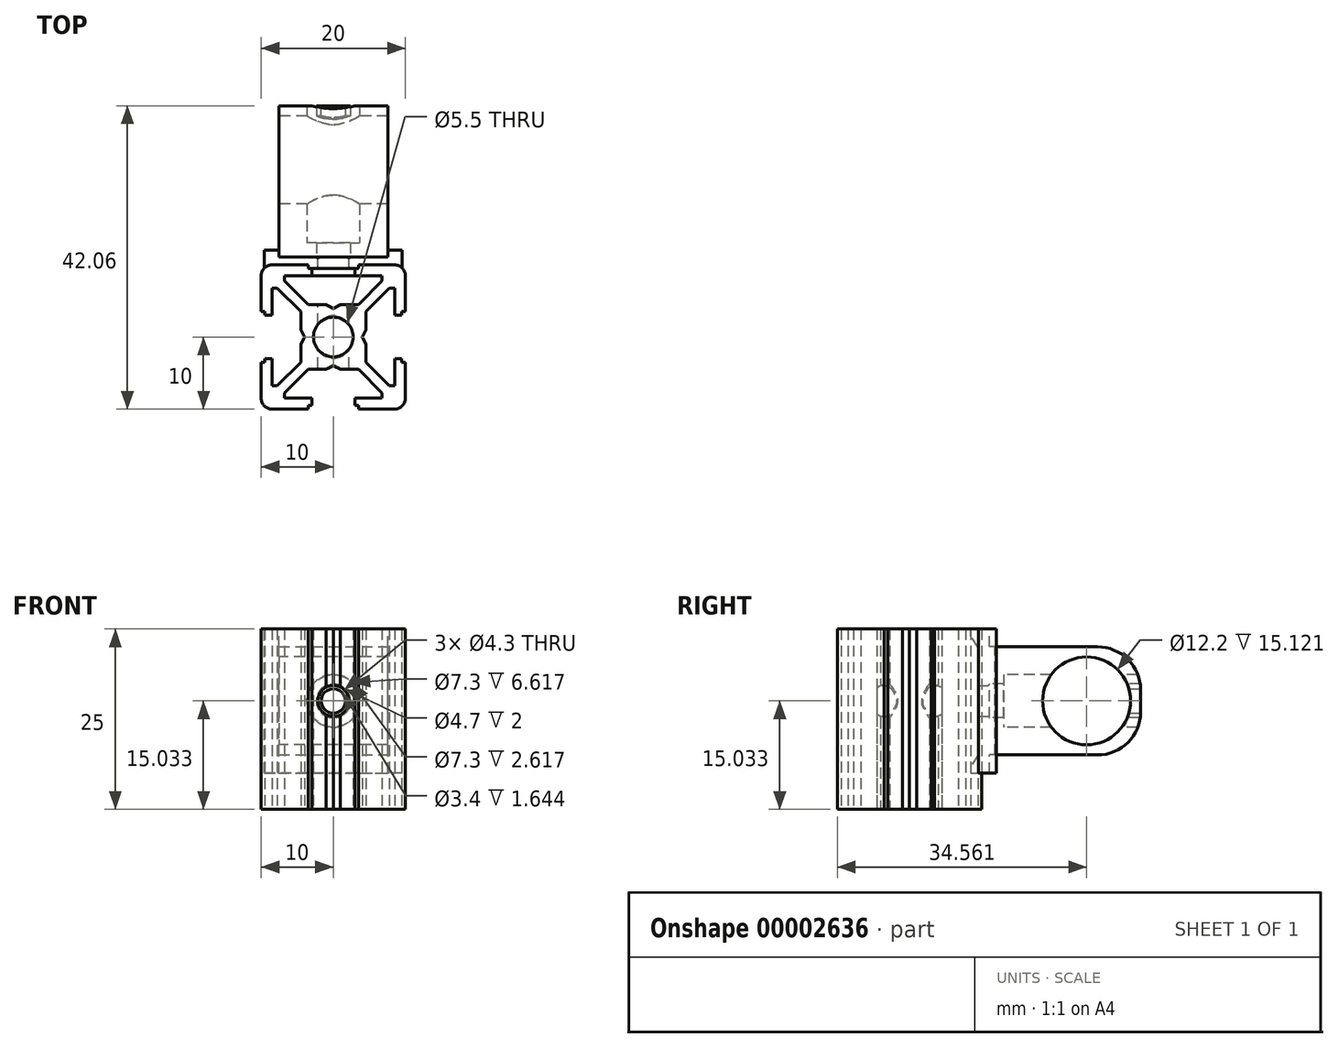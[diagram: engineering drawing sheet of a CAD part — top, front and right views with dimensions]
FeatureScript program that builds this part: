
annotation { "Feature Type Name" : "Feature", "Feature Type Description" : "" }
export const myFeature = defineFeature(function(context is Context, id is Id, definition is map)
    precondition{}
    {
        {
            var Q0;
            Q0=qCreatedBy(makeId("Top.planeOp"),FACE);
            var sketch = newSketch(context, id + "F0", { "sketchPlane" : qUnion([Q0])});
            skLineSegment(sketch, "E0", {"start": v(-1, -4.5) * mm, "end": v(-3.5, -4.5) * mm});
            skLineSegment(sketch, "E1", {"start": v(-6.77, -7.77) * mm, "end": v(-6.77, -8.5) * mm});
            skLineSegment(sketch, "E2", {"start": v(-6.77, -8.5) * mm, "end": v(-3, -8.5) * mm});
            skLineSegment(sketch, "E3", {"start": v(-3, -8.5) * mm, "end": v(-3, -9.5) * mm});
            skLineSegment(sketch, "E4", {"start": v(-5.56, -10) * mm, "end": v(-8.5, -10) * mm});
            skLineSegment(sketch, "E5", {"start": v(-1, -4.5) * mm, "end": v(0, -4) * mm});
            skLineSegment(sketch, "E6", {"start": v(-3, -9.5) * mm, "end": v(-3.5, -9.5) * mm});
            skLineSegment(sketch, "E7", {"start": v(-3.5, -9.5) * mm, "end": v(-3.5, -10) * mm, "construction": true});
            skArc(sketch, "E8.filletArc", {"start": v(-9.56, -9.56) * mm, "mid": v(-9.07, -9.89) * mm, "end": v(-8.5, -10) * mm});
            skLineSegment(sketch, "E9", {"start": v(-3.5, -10) * mm, "end": v(-5.56, -10) * mm});
            skPoint(sketch, "E10.orphan", {"position": v(0, -10) * mm});
            skLineSegment(sketch, "E11.trimOffspring", {"start": v(-8.5, -8.5) * mm, "end": v(-1.94, -1.94) * mm});
            skPoint(sketch, "E12", {"position": v(0, -4.5) * mm});
            skLineSegment(sketch, "E13", {"start": v(-3.5, -4.5) * mm, "end": v(-6.77, -7.77) * mm});
            skArc(sketch, "E14", {"start": v(-1.94, -1.94) * mm, "mid": v(-1.05, -2.54) * mm, "end": v(0, -2.75) * mm});
            skPoint(sketch, "E15", {"position": v(-1.94, -1.94) * mm});
            skLineSegment(sketch, "E16", {"start": v(0, -4) * mm, "end": v(0, -2.75) * mm});
            skLineSegment(sketch, "E17", {"start": v(-9.56, -9.56) * mm, "end": v(-8.5, -8.5) * mm});
            skPoint(sketch, "E18", {"position": v(-5.56, -10) * mm});
            skLineSegment(sketch, "E19", {"start": v(-3.5, -9.5) * mm, "end": v(-3.5, -10) * mm});
            skPoint(sketch, "E20.0.MirrorP", {"position": v(-10, -5.56) * mm});
            skPoint(sketch, "E20.1.MirrorP", {"position": v(-10, -5.56) * mm});
            skPoint(sketch, "E20.2.MirrorP", {"position": v(-10, -5.56) * mm});
            skPoint(sketch, "E20.3.MirrorP", {"position": v(-10, -5.56) * mm});
            skPoint(sketch, "E20.4.MirrorP", {"position": v(-10, -5.56) * mm});
            skPoint(sketch, "E20.5.MirrorP", {"position": v(-10, -5.56) * mm});
            skPoint(sketch, "E20.6.MirrorP", {"position": v(-10, -5.56) * mm});
            skPoint(sketch, "E20.7.MirrorP", {"position": v(-10, -5.56) * mm});
            skPoint(sketch, "E20.8.MirrorP", {"position": v(-10, -5.56) * mm});
            skPoint(sketch, "E20.9.MirrorP", {"position": v(-10, -5.56) * mm});
            skPoint(sketch, "E20.10.MirrorP", {"position": v(-10, -5.56) * mm});
            skLineSegment(sketch, "E20.11.MirrorCS", {"start": v(-9.5, -3.5) * mm, "end": v(-10, -3.5) * mm, "construction": true});
            skPoint(sketch, "E20.12.MirrorP", {"position": v(-10, -5.56) * mm});
            skLineSegment(sketch, "E20.13.MirrorCS", {"start": v(-9.5, -3.5) * mm, "end": v(-10, -3.5) * mm});
            skLineSegment(sketch, "E20.14.MirrorCS", {"start": v(-7.77, -6.77) * mm, "end": v(-8.5, -6.77) * mm});
            skPoint(sketch, "E20.15.MirrorP", {"position": v(-10, -5.56) * mm});
            skLineSegment(sketch, "E20.16.MirrorCS", {"start": v(-9.5, -3) * mm, "end": v(-9.5, -3.5) * mm});
            skPoint(sketch, "E20.17.MirrorP", {"position": v(-10, 0) * mm});
            skLineSegment(sketch, "E20.18.MirrorCS", {"start": v(-10, -5.56) * mm, "end": v(-10, -8.5) * mm});
            skArc(sketch, "E20.19.MirrorCS", {"start": v(-1.94, -1.94) * mm, "mid": v(-2.54, -1.05) * mm, "end": v(-2.75, 0) * mm});
            skPoint(sketch, "E20.20.MirrorP", {"position": v(-4.5, 0) * mm});
            skLineSegment(sketch, "E20.21.MirrorCS", {"start": v(-4.5, -3.5) * mm, "end": v(-7.77, -6.77) * mm});
            skLineSegment(sketch, "E20.23.MirrorCS", {"start": v(-4.5, -1) * mm, "end": v(-4.5, -3.5) * mm});
            skLineSegment(sketch, "E20.24.MirrorCS", {"start": v(-8.5, -6.77) * mm, "end": v(-8.5, -3) * mm});
            skLineSegment(sketch, "E20.25.MirrorCS", {"start": v(-10, -3.5) * mm, "end": v(-10, -5.56) * mm});
            skLineSegment(sketch, "E20.26.MirrorCS", {"start": v(-4, 0) * mm, "end": v(-2.75, 0) * mm});
            skArc(sketch, "E20.28.MirrorCS", {"start": v(-9.56, -9.56) * mm, "mid": v(-9.89, -9.07) * mm, "end": v(-10, -8.5) * mm});
            skLineSegment(sketch, "E20.29.MirrorCS", {"start": v(-4.5, -1) * mm, "end": v(-4, 0) * mm});
            skLineSegment(sketch, "E20.30.MirrorCS", {"start": v(-10, -5.56) * mm, "end": v(-10, -8.5) * mm});
            skPoint(sketch, "E20.31.MirrorP", {"position": v(-10, -5.56) * mm});
            skLineSegment(sketch, "E20.32.MirrorCS", {"start": v(-8.5, -3) * mm, "end": v(-9.5, -3) * mm});
            skPoint(sketch, "E21.0.MirrorP", {"position": v(-5.56, 10) * mm});
            skPoint(sketch, "E21.1.MirrorP", {"position": v(-10, 5.56) * mm});
            skPoint(sketch, "E21.2.MirrorP", {"position": v(-5.56, 10) * mm});
            skPoint(sketch, "E21.3.MirrorP", {"position": v(-10, 5.56) * mm});
            skPoint(sketch, "E21.4.MirrorP", {"position": v(-5.56, 10) * mm});
            skPoint(sketch, "E21.5.MirrorP", {"position": v(-10, 5.56) * mm});
            skPoint(sketch, "E21.6.MirrorP", {"position": v(-10, 5.56) * mm});
            skPoint(sketch, "E21.7.MirrorP", {"position": v(-5.56, 10) * mm});
            skPoint(sketch, "E21.8.MirrorP", {"position": v(-5.56, 10) * mm});
            skPoint(sketch, "E21.9.MirrorP", {"position": v(-10, 5.56) * mm});
            skPoint(sketch, "E21.10.MirrorP", {"position": v(-5.56, 10) * mm});
            skPoint(sketch, "E21.11.MirrorP", {"position": v(-10, 5.56) * mm});
            skPoint(sketch, "E21.12.MirrorP", {"position": v(-5.56, 10) * mm});
            skPoint(sketch, "E21.13.MirrorP", {"position": v(-10, 5.56) * mm});
            skPoint(sketch, "E21.14.MirrorP", {"position": v(-5.56, 10) * mm});
            skPoint(sketch, "E21.15.MirrorP", {"position": v(-10, 5.56) * mm});
            skPoint(sketch, "E21.16.MirrorP", {"position": v(-5.56, 10) * mm});
            skPoint(sketch, "E21.17.MirrorP", {"position": v(-10, 5.56) * mm});
            skLineSegment(sketch, "E21.18.MirrorCS", {"start": v(-9.5, 3.5) * mm, "end": v(-10, 3.5) * mm, "construction": true});
            skPoint(sketch, "E21.19.MirrorP", {"position": v(-5.56, 10) * mm});
            skPoint(sketch, "E21.20.MirrorP", {"position": v(-10, 5.56) * mm});
            skLineSegment(sketch, "E21.21.MirrorCS", {"start": v(-3.5, 9.5) * mm, "end": v(-3.5, 10) * mm, "construction": true});
            skLineSegment(sketch, "E21.22.MirrorCS", {"start": v(-3.5, 9.5) * mm, "end": v(-3.5, 10) * mm});
            skPoint(sketch, "E21.23.MirrorP", {"position": v(-5.56, 10) * mm});
            skLineSegment(sketch, "E21.24.MirrorCS", {"start": v(-9.5, 3.5) * mm, "end": v(-10, 3.5) * mm});
            skPoint(sketch, "E21.25.MirrorP", {"position": v(-10, 5.56) * mm});
            skPoint(sketch, "E21.26.MirrorP", {"position": v(-5.56, 10) * mm});
            skPoint(sketch, "E21.27.MirrorP", {"position": v(-10, 5.56) * mm});
            skLineSegment(sketch, "E21.28.MirrorCS", {"start": v(-3, 9.5) * mm, "end": v(-3.5, 9.5) * mm});
            skLineSegment(sketch, "E21.29.MirrorCS", {"start": v(-9.5, 3) * mm, "end": v(-9.5, 3.5) * mm});
            skLineSegment(sketch, "E21.30.MirrorCS", {"start": v(-8.5, 3) * mm, "end": v(-9.5, 3) * mm});
            skPoint(sketch, "E21.31.MirrorP", {"position": v(-5.56, 10) * mm});
            skPoint(sketch, "E21.32.MirrorP", {"position": v(-10, 5.56) * mm});
            skLineSegment(sketch, "E21.34.MirrorCS", {"start": v(-10, 3.5) * mm, "end": v(-10, 5.56) * mm});
            skArc(sketch, "E21.35.MirrorCS", {"start": v(-9.56, 9.56) * mm, "mid": v(-9.89, 9.07) * mm, "end": v(-10, 8.5) * mm});
            skLineSegment(sketch, "E21.36.MirrorCS", {"start": v(-8.5, 6.77) * mm, "end": v(-8.5, 3) * mm});
            skLineSegment(sketch, "E21.37.MirrorCS", {"start": v(-4.5, 1) * mm, "end": v(-4, 0) * mm});
            skLineSegment(sketch, "E21.38.MirrorCS", {"start": v(-10, 5.56) * mm, "end": v(-10, 8.5) * mm});
            skLineSegment(sketch, "E21.40.MirrorCS", {"start": v(-4.5, 3.5) * mm, "end": v(-7.77, 6.77) * mm});
            skLineSegment(sketch, "E21.41.MirrorCS", {"start": v(-4.5, 1) * mm, "end": v(-4.5, 3.5) * mm});
            skLineSegment(sketch, "E21.42.MirrorCS", {"start": v(-1, 4.5) * mm, "end": v(-3.5, 4.5) * mm});
            skLineSegment(sketch, "E21.43.MirrorCS", {"start": v(-6.77, 8.5) * mm, "end": v(-3, 8.5) * mm});
            skLineSegment(sketch, "E21.44.MirrorCS", {"start": v(-6.77, 7.77) * mm, "end": v(-6.77, 8.5) * mm});
            skLineSegment(sketch, "E21.45.MirrorCS", {"start": v(-5.56, 10) * mm, "end": v(-8.5, 10) * mm});
            skLineSegment(sketch, "E21.46.MirrorCS", {"start": v(-3, 8.5) * mm, "end": v(-3, 9.5) * mm});
            skLineSegment(sketch, "E21.47.MirrorCS", {"start": v(-1, 4.5) * mm, "end": v(0, 4) * mm});
            skLineSegment(sketch, "E21.48.MirrorCS", {"start": v(-5.56, 10) * mm, "end": v(-8.5, 10) * mm});
            skLineSegment(sketch, "E21.49.MirrorCS", {"start": v(-3.5, 10) * mm, "end": v(-5.56, 10) * mm});
            skArc(sketch, "E21.50.MirrorCS", {"start": v(-9.56, 9.56) * mm, "mid": v(-9.07, 9.89) * mm, "end": v(-8.5, 10) * mm});
            skLineSegment(sketch, "E21.51.MirrorCS", {"start": v(-3.5, 4.5) * mm, "end": v(-6.77, 7.77) * mm});
            skLineSegment(sketch, "E21.52.MirrorCS", {"start": v(-8.5, 8.5) * mm, "end": v(-1.94, 1.94) * mm});
            skLineSegment(sketch, "E21.53.MirrorCS", {"start": v(-9.56, 9.56) * mm, "end": v(-8.5, 8.5) * mm});
            skLineSegment(sketch, "E21.54.MirrorCS", {"start": v(-9.56, 9.56) * mm, "end": v(-8.5, 8.5) * mm});
            skLineSegment(sketch, "E21.55.MirrorCS", {"start": v(0, 4) * mm, "end": v(0, 2.75) * mm});
            skArc(sketch, "E21.56.MirrorCS", {"start": v(-1.94, 1.94) * mm, "mid": v(-1.05, 2.54) * mm, "end": v(0, 2.75) * mm});
            skPoint(sketch, "E21.58.MirrorP", {"position": v(0, 4.5) * mm});
            skLineSegment(sketch, "E21.59.MirrorCS", {"start": v(-7.77, 6.77) * mm, "end": v(-8.5, 6.77) * mm});
            skPoint(sketch, "E21.60.MirrorP", {"position": v(-5.56, 10) * mm});
            skArc(sketch, "E21.61.MirrorCS", {"start": v(-1.94, 1.94) * mm, "mid": v(-2.54, 1.05) * mm, "end": v(-2.75, 0) * mm});
            skPoint(sketch, "E21.62.MirrorP", {"position": v(0, 10) * mm});
            skPoint(sketch, "E21.63.MirrorP", {"position": v(-1.94, 1.94) * mm});
            skPoint(sketch, "E21.64.MirrorP", {"position": v(-1.94, 1.94) * mm});
            skLineSegment(sketch, "E21.65.MirrorCS", {"start": v(-10, 5.56) * mm, "end": v(-10, 8.5) * mm});
            skPoint(sketch, "E21.66.MirrorP", {"position": v(-10, 5.56) * mm});
            skPoint(sketch, "E22.0.MirrorP", {"position": v(10, 5.56) * mm});
            skPoint(sketch, "E22.1.MirrorP", {"position": v(5.56, -10) * mm});
            skPoint(sketch, "E22.2.MirrorP", {"position": v(5.56, 10) * mm});
            skPoint(sketch, "E22.3.MirrorP", {"position": v(10, 5.56) * mm});
            skPoint(sketch, "E22.4.MirrorP", {"position": v(10, -5.56) * mm});
            skPoint(sketch, "E22.5.MirrorP", {"position": v(5.56, -10) * mm});
            skPoint(sketch, "E22.6.MirrorP", {"position": v(5.56, -10) * mm});
            skPoint(sketch, "E22.7.MirrorP", {"position": v(10, 5.56) * mm});
            skPoint(sketch, "E22.8.MirrorP", {"position": v(5.56, 10) * mm});
            skPoint(sketch, "E22.9.MirrorP", {"position": v(10, -5.56) * mm});
            skPoint(sketch, "E22.10.MirrorP", {"position": v(10, 5.56) * mm});
            skPoint(sketch, "E22.11.MirrorP", {"position": v(5.56, -10) * mm});
            skPoint(sketch, "E22.12.MirrorP", {"position": v(5.56, 10) * mm});
            skPoint(sketch, "E22.13.MirrorP", {"position": v(10, -5.56) * mm});
            skPoint(sketch, "E22.14.MirrorP", {"position": v(10, 5.56) * mm});
            skPoint(sketch, "E22.15.MirrorP", {"position": v(5.56, -10) * mm});
            skPoint(sketch, "E22.16.MirrorP", {"position": v(10, -5.56) * mm});
            skPoint(sketch, "E22.17.MirrorP", {"position": v(5.56, 10) * mm});
            skPoint(sketch, "E22.18.MirrorP", {"position": v(5.56, -10) * mm});
            skPoint(sketch, "E22.19.MirrorP", {"position": v(5.56, 10) * mm});
            skPoint(sketch, "E22.20.MirrorP", {"position": v(10, 5.56) * mm});
            skPoint(sketch, "E22.21.MirrorP", {"position": v(10, -5.56) * mm});
            skPoint(sketch, "E22.22.MirrorP", {"position": v(10, -5.56) * mm});
            skPoint(sketch, "E22.23.MirrorP", {"position": v(5.56, -10) * mm});
            skPoint(sketch, "E22.24.MirrorP", {"position": v(10, 5.56) * mm});
            skPoint(sketch, "E22.25.MirrorP", {"position": v(5.56, 10) * mm});
            skPoint(sketch, "E22.26.MirrorP", {"position": v(10, -5.56) * mm});
            skPoint(sketch, "E22.27.MirrorP", {"position": v(10, 5.56) * mm});
            skPoint(sketch, "E22.28.MirrorP", {"position": v(5.56, -10) * mm});
            skPoint(sketch, "E22.29.MirrorP", {"position": v(5.56, 10) * mm});
            skPoint(sketch, "E22.30.MirrorP", {"position": v(10, -5.56) * mm});
            skPoint(sketch, "E22.31.MirrorP", {"position": v(5.56, 10) * mm});
            skPoint(sketch, "E22.32.MirrorP", {"position": v(5.56, -10) * mm});
            skPoint(sketch, "E22.33.MirrorP", {"position": v(10, 5.56) * mm});
            skPoint(sketch, "E22.34.MirrorP", {"position": v(10, 5.56) * mm});
            skPoint(sketch, "E22.35.MirrorP", {"position": v(5.56, 10) * mm});
            skPoint(sketch, "E22.36.MirrorP", {"position": v(10, -5.56) * mm});
            skPoint(sketch, "E22.37.MirrorP", {"position": v(5.56, -10) * mm});
            skLineSegment(sketch, "E22.38.MirrorCS", {"start": v(3.5, 9.5) * mm, "end": v(3.5, 10) * mm, "construction": true});
            skLineSegment(sketch, "E22.39.MirrorCS", {"start": v(9.5, 3.5) * mm, "end": v(10, 3.5) * mm, "construction": true});
            skLineSegment(sketch, "E22.40.MirrorCS", {"start": v(9.5, -3.5) * mm, "end": v(10, -3.5) * mm, "construction": true});
            skLineSegment(sketch, "E22.41.MirrorCS", {"start": v(3.5, -9.5) * mm, "end": v(3.5, -10) * mm, "construction": true});
            skPoint(sketch, "E22.42.MirrorP", {"position": v(10, 5.56) * mm});
            skPoint(sketch, "E22.43.MirrorP", {"position": v(10, -5.56) * mm});
            skPoint(sketch, "E22.44.MirrorP", {"position": v(5.56, -10) * mm});
            skPoint(sketch, "E22.45.MirrorP", {"position": v(5.56, 10) * mm});
            skLineSegment(sketch, "E22.46.MirrorCS", {"start": v(9.5, 3.5) * mm, "end": v(10, 3.5) * mm});
            skLineSegment(sketch, "E22.47.MirrorCS", {"start": v(9.5, -3) * mm, "end": v(9.5, -3.5) * mm});
            skLineSegment(sketch, "E22.48.MirrorCS", {"start": v(9.5, -3.5) * mm, "end": v(10, -3.5) * mm});
            skLineSegment(sketch, "E22.49.MirrorCS", {"start": v(9.56, -9.56) * mm, "end": v(8.5, -8.5) * mm});
            skLineSegment(sketch, "E22.50.MirrorCS", {"start": v(3, -9.5) * mm, "end": v(3.5, -9.5) * mm});
            skPoint(sketch, "E22.51.MirrorP", {"position": v(10, -5.56) * mm});
            skPoint(sketch, "E22.52.MirrorP", {"position": v(10, 5.56) * mm});
            skPoint(sketch, "E22.53.MirrorP", {"position": v(5.56, 10) * mm});
            skPoint(sketch, "E22.54.MirrorP", {"position": v(5.56, -10) * mm});
            skLineSegment(sketch, "E22.55.MirrorCS", {"start": v(3, 9.5) * mm, "end": v(3.5, 9.5) * mm});
            skLineSegment(sketch, "E22.56.MirrorCS", {"start": v(9.5, 3) * mm, "end": v(9.5, 3.5) * mm});
            skLineSegment(sketch, "E22.57.MirrorCS", {"start": v(3.5, -9.5) * mm, "end": v(3.5, -10) * mm});
            skLineSegment(sketch, "E22.58.MirrorCS", {"start": v(3.5, 9.5) * mm, "end": v(3.5, 10) * mm});
            skLineSegment(sketch, "E22.59.MirrorCS", {"start": v(3, 8.5) * mm, "end": v(3, 9.5) * mm});
            skLineSegment(sketch, "E22.60.MirrorCS", {"start": v(6.77, 7.77) * mm, "end": v(6.77, 8.5) * mm});
            skPoint(sketch, "E22.61.MirrorP", {"position": v(5.56, 10) * mm});
            skLineSegment(sketch, "E22.62.MirrorCS", {"start": v(6.77, -7.77) * mm, "end": v(6.77, -8.5) * mm});
            skPoint(sketch, "E22.63.MirrorP", {"position": v(5.56, -10) * mm});
            skPoint(sketch, "E22.64.MirrorP", {"position": v(10, -5.56) * mm});
            skLineSegment(sketch, "E22.65.MirrorCS", {"start": v(9.56, -9.56) * mm, "end": v(8.5, -8.5) * mm});
            skLineSegment(sketch, "E22.66.MirrorCS", {"start": v(7.77, 6.77) * mm, "end": v(8.5, 6.77) * mm});
            skLineSegment(sketch, "E22.67.MirrorCS", {"start": v(1, 4.5) * mm, "end": v(0, 4) * mm});
            skLineSegment(sketch, "E22.68.MirrorCS", {"start": v(4.5, -1) * mm, "end": v(4, 0) * mm});
            skLineSegment(sketch, "E22.69.MirrorCS", {"start": v(4, 0) * mm, "end": v(2.75, 0) * mm});
            skLineSegment(sketch, "E22.70.MirrorCS", {"start": v(1, -4.5) * mm, "end": v(0, -4) * mm});
            skLineSegment(sketch, "E22.71.MirrorCS", {"start": v(10, 5.56) * mm, "end": v(10, 8.5) * mm});
            skPoint(sketch, "E22.72.MirrorP", {"position": v(10, 5.56) * mm});
            skPoint(sketch, "E22.73.MirrorP", {"position": v(10, 0) * mm});
            skLineSegment(sketch, "E22.74.MirrorCS", {"start": v(9.56, 9.56) * mm, "end": v(8.5, 8.5) * mm});
            skLineSegment(sketch, "E22.75.MirrorCS", {"start": v(4.5, 1) * mm, "end": v(4, 0) * mm});
            skLineSegment(sketch, "E22.76.MirrorCS", {"start": v(7.77, -6.77) * mm, "end": v(8.5, -6.77) * mm});
            skLineSegment(sketch, "E22.78.MirrorCS", {"start": v(10, 5.56) * mm, "end": v(10, 8.5) * mm});
            skLineSegment(sketch, "E22.79.MirrorCS", {"start": v(3.5, -10) * mm, "end": v(5.56, -10) * mm});
            skLineSegment(sketch, "E22.80.MirrorCS", {"start": v(3, -8.5) * mm, "end": v(3, -9.5) * mm});
            skLineSegment(sketch, "E22.81.MirrorCS", {"start": v(5.56, -10) * mm, "end": v(8.5, -10) * mm});
            skPoint(sketch, "E22.83.MirrorP", {"position": v(5.56, -10) * mm});
            skLineSegment(sketch, "E22.84.MirrorCS", {"start": v(8.5, 3) * mm, "end": v(9.5, 3) * mm});
            skLineSegment(sketch, "E22.85.MirrorCS", {"start": v(3.5, 10) * mm, "end": v(5.56, 10) * mm});
            skArc(sketch, "E22.86.MirrorCS", {"start": v(1.94, -1.94) * mm, "mid": v(1.05, -2.54) * mm, "end": v(0, -2.75) * mm});
            skPoint(sketch, "E22.87.MirrorP", {"position": v(1.94, -1.94) * mm});
            skPoint(sketch, "E22.88.MirrorP", {"position": v(4.5, 0) * mm});
            skArc(sketch, "E22.89.MirrorCS", {"start": v(9.56, 9.56) * mm, "mid": v(9.07, 9.89) * mm, "end": v(8.5, 10) * mm});
            skLineSegment(sketch, "E22.90.MirrorCS", {"start": v(10, 3.5) * mm, "end": v(10, 5.56) * mm});
            skLineSegment(sketch, "E22.91.MirrorCS", {"start": v(8.5, -8.5) * mm, "end": v(1.94, -1.94) * mm});
            skLineSegment(sketch, "E22.92.MirrorCS", {"start": v(3.5, -4.5) * mm, "end": v(6.77, -7.77) * mm});
            skArc(sketch, "E22.93.MirrorCS", {"start": v(9.56, -9.56) * mm, "mid": v(9.07, -9.89) * mm, "end": v(8.5, -10) * mm});
            skLineSegment(sketch, "E22.94.MirrorCS", {"start": v(6.77, 8.5) * mm, "end": v(3, 8.5) * mm});
            skLineSegment(sketch, "E22.95.MirrorCS", {"start": v(4.5, 1) * mm, "end": v(4.5, 3.5) * mm});
            skLineSegment(sketch, "E22.96.MirrorCS", {"start": v(10, -5.56) * mm, "end": v(10, -8.5) * mm});
            skLineSegment(sketch, "E22.97.MirrorCS", {"start": v(5.56, -10) * mm, "end": v(8.5, -10) * mm});
            skPoint(sketch, "E22.99.MirrorP", {"position": v(5.56, 10) * mm});
            skLineSegment(sketch, "E22.101.MirrorCS", {"start": v(10, -5.56) * mm, "end": v(10, -8.5) * mm});
            skPoint(sketch, "E22.103.MirrorP", {"position": v(4.5, 0) * mm});
            skArc(sketch, "E22.104.MirrorCS", {"start": v(1.94, 1.94) * mm, "mid": v(1.05, 2.54) * mm, "end": v(0, 2.75) * mm});
            skArc(sketch, "E22.105.MirrorCS", {"start": v(1.94, -1.94) * mm, "mid": v(2.54, -1.05) * mm, "end": v(2.75, 0) * mm});
            skLineSegment(sketch, "E22.106.MirrorCS", {"start": v(4.5, 3.5) * mm, "end": v(7.77, 6.77) * mm});
            skLineSegment(sketch, "E22.107.MirrorCS", {"start": v(8.5, 8.5) * mm, "end": v(1.94, 1.94) * mm});
            skLineSegment(sketch, "E22.108.MirrorCS", {"start": v(8.5, -6.77) * mm, "end": v(8.5, -3) * mm});
            skArc(sketch, "E22.109.MirrorCS", {"start": v(9.56, -9.56) * mm, "mid": v(9.89, -9.07) * mm, "end": v(10, -8.5) * mm});
            skPoint(sketch, "E22.110.MirrorP", {"position": v(1.94, 1.94) * mm});
            skLineSegment(sketch, "E22.111.MirrorCS", {"start": v(6.77, -8.5) * mm, "end": v(3, -8.5) * mm});
            skLineSegment(sketch, "E22.112.MirrorCS", {"start": v(1, -4.5) * mm, "end": v(3.5, -4.5) * mm});
            skLineSegment(sketch, "E22.113.MirrorCS", {"start": v(4.5, -1) * mm, "end": v(4.5, -3.5) * mm});
            skLineSegment(sketch, "E22.114.MirrorCS", {"start": v(3.5, 4.5) * mm, "end": v(6.77, 7.77) * mm});
            skPoint(sketch, "E22.115.MirrorP", {"position": v(10, -5.56) * mm});
            skLineSegment(sketch, "E22.116.MirrorCS", {"start": v(9.56, 9.56) * mm, "end": v(8.5, 8.5) * mm});
            skLineSegment(sketch, "E22.117.MirrorCS", {"start": v(4, 0) * mm, "end": v(2.75, 0) * mm});
            skArc(sketch, "E22.118.MirrorCS", {"start": v(9.56, 9.56) * mm, "mid": v(9.89, 9.07) * mm, "end": v(10, 8.5) * mm});
            skPoint(sketch, "E22.119.MirrorP", {"position": v(5.56, 10) * mm});
            skLineSegment(sketch, "E22.120.MirrorCS", {"start": v(8.5, -3) * mm, "end": v(9.5, -3) * mm});
            skLineSegment(sketch, "E22.121.MirrorCS", {"start": v(1, 4.5) * mm, "end": v(3.5, 4.5) * mm});
            skArc(sketch, "E22.122.MirrorCS", {"start": v(1.94, 1.94) * mm, "mid": v(2.54, 1.05) * mm, "end": v(2.75, 0) * mm});
            skLineSegment(sketch, "E22.123.MirrorCS", {"start": v(5.56, 10) * mm, "end": v(8.5, 10) * mm});
            skPoint(sketch, "E22.124.MirrorP", {"position": v(10, 0) * mm});
            skLineSegment(sketch, "E22.125.MirrorCS", {"start": v(10, -3.5) * mm, "end": v(10, -5.56) * mm});
            skLineSegment(sketch, "E22.126.MirrorCS", {"start": v(5.56, 10) * mm, "end": v(8.5, 10) * mm});
            skLineSegment(sketch, "E22.127.MirrorCS", {"start": v(4.5, -3.5) * mm, "end": v(7.77, -6.77) * mm});
            skPoint(sketch, "E22.128.MirrorP", {"position": v(10, -5.56) * mm});
            skPoint(sketch, "E22.129.MirrorP", {"position": v(1.94, -1.94) * mm});
            skPoint(sketch, "E22.131.MirrorP", {"position": v(1.94, 1.94) * mm});
            skLineSegment(sketch, "E22.132.MirrorCS", {"start": v(8.5, 6.77) * mm, "end": v(8.5, 3) * mm});
            skPoint(sketch, "E22.133.MirrorP", {"position": v(10, 5.56) * mm});
            skSolve(sketch);
        }
        {
            var Q0;
            Q0=qSketchRegion(id+"F0",true);
            extrude(context, id + "F1", {"entities" : qUnion([Q0]), "depth" : 25 * mm});
        }
        {
            var Q0;
            Q0=makeQuery(id+"F1.opExtrude","CAP_FACE",FACE,{"disambiguationData":[OSD([sQuery(id+"F0.wireOp",EDGE,"E0"),sQuery(id+"F0.wireOp",EDGE,"E1"),sQuery(id+"F0.wireOp",EDGE,"E2"),sQuery(id+"F0.wireOp",EDGE,"E3"),sQuery(id+"F0.wireOp",EDGE,"E5"),sQuery(id+"F0.wireOp",EDGE,"E6"),sQuery(id+"F0.wireOp",EDGE,"E4"),sQuery(id+"F0.wireOp",EDGE,"E8.filletArc"),sQuery(id+"F0.wireOp",EDGE,"E13"),sQuery(id+"F0.wireOp",EDGE,"E14"),sQuery(id+"F0.wireOp",EDGE,"E19"),sQuery(id+"F0.wireOp",EDGE,"E20.13.MirrorCS"),sQuery(id+"F0.wireOp",EDGE,"E20.14.MirrorCS"),sQuery(id+"F0.wireOp",EDGE,"E20.16.MirrorCS"),sQuery(id+"F0.wireOp",EDGE,"E20.19.MirrorCS"),sQuery(id+"F0.wireOp",EDGE,"E20.21.MirrorCS"),sQuery(id+"F0.wireOp",EDGE,"E20.23.MirrorCS"),sQuery(id+"F0.wireOp",EDGE,"E20.24.MirrorCS"),sQuery(id+"F0.wireOp",EDGE,"E20.25.MirrorCS"),sQuery(id+"F0.wireOp",EDGE,"E20.28.MirrorCS"),sQuery(id+"F0.wireOp",EDGE,"E20.29.MirrorCS"),sQuery(id+"F0.wireOp",EDGE,"E20.32.MirrorCS"),sQuery(id+"F0.wireOp",EDGE,"E21.22.MirrorCS"),sQuery(id+"F0.wireOp",EDGE,"E21.24.MirrorCS"),sQuery(id+"F0.wireOp",EDGE,"E21.28.MirrorCS"),sQuery(id+"F0.wireOp",EDGE,"E21.29.MirrorCS"),sQuery(id+"F0.wireOp",EDGE,"E21.30.MirrorCS"),sQuery(id+"F0.wireOp",EDGE,"E21.35.MirrorCS"),sQuery(id+"F0.wireOp",EDGE,"E21.36.MirrorCS"),sQuery(id+"F0.wireOp",EDGE,"E21.37.MirrorCS"),sQuery(id+"F0.wireOp",EDGE,"E21.40.MirrorCS"),sQuery(id+"F0.wireOp",EDGE,"E21.41.MirrorCS"),sQuery(id+"F0.wireOp",EDGE,"E21.42.MirrorCS"),sQuery(id+"F0.wireOp",EDGE,"E21.43.MirrorCS"),sQuery(id+"F0.wireOp",EDGE,"E21.44.MirrorCS"),sQuery(id+"F0.wireOp",EDGE,"E21.46.MirrorCS"),sQuery(id+"F0.wireOp",EDGE,"E21.47.MirrorCS"),sQuery(id+"F0.wireOp",EDGE,"E21.49.MirrorCS"),sQuery(id+"F0.wireOp",EDGE,"E21.50.MirrorCS"),sQuery(id+"F0.wireOp",EDGE,"E21.51.MirrorCS"),sQuery(id+"F0.wireOp",EDGE,"E21.56.MirrorCS"),sQuery(id+"F0.wireOp",EDGE,"E21.59.MirrorCS"),sQuery(id+"F0.wireOp",EDGE,"E21.61.MirrorCS"),sQuery(id+"F0.wireOp",EDGE,"E21.65.MirrorCS"),sQuery(id+"F0.wireOp",EDGE,"E22.46.MirrorCS"),sQuery(id+"F0.wireOp",EDGE,"E22.47.MirrorCS"),sQuery(id+"F0.wireOp",EDGE,"E22.48.MirrorCS"),sQuery(id+"F0.wireOp",EDGE,"E22.50.MirrorCS"),sQuery(id+"F0.wireOp",EDGE,"E22.55.MirrorCS"),sQuery(id+"F0.wireOp",EDGE,"E22.56.MirrorCS"),sQuery(id+"F0.wireOp",EDGE,"E22.57.MirrorCS"),sQuery(id+"F0.wireOp",EDGE,"E22.58.MirrorCS"),sQuery(id+"F0.wireOp",EDGE,"E22.60.MirrorCS"),sQuery(id+"F0.wireOp",EDGE,"E22.80.MirrorCS"),sQuery(id+"F0.wireOp",EDGE,"E22.62.MirrorCS"),sQuery(id+"F0.wireOp",EDGE,"E22.66.MirrorCS"),sQuery(id+"F0.wireOp",EDGE,"E22.67.MirrorCS"),sQuery(id+"F0.wireOp",EDGE,"E22.68.MirrorCS"),sQuery(id+"F0.wireOp",EDGE,"E22.70.MirrorCS"),sQuery(id+"F0.wireOp",EDGE,"E22.75.MirrorCS"),sQuery(id+"F0.wireOp",EDGE,"E22.76.MirrorCS"),sQuery(id+"F0.wireOp",EDGE,"E22.59.MirrorCS"),sQuery(id+"F0.wireOp",EDGE,"E22.79.MirrorCS"),sQuery(id+"F0.wireOp",EDGE,"E22.84.MirrorCS"),sQuery(id+"F0.wireOp",EDGE,"E22.86.MirrorCS"),sQuery(id+"F0.wireOp",EDGE,"E22.89.MirrorCS"),sQuery(id+"F0.wireOp",EDGE,"E22.90.MirrorCS"),sQuery(id+"F0.wireOp",EDGE,"E22.92.MirrorCS"),sQuery(id+"F0.wireOp",EDGE,"E22.93.MirrorCS"),sQuery(id+"F0.wireOp",EDGE,"E22.94.MirrorCS"),sQuery(id+"F0.wireOp",EDGE,"E22.95.MirrorCS"),sQuery(id+"F0.wireOp",EDGE,"E22.96.MirrorCS"),sQuery(id+"F0.wireOp",EDGE,"E22.104.MirrorCS"),sQuery(id+"F0.wireOp",EDGE,"E22.105.MirrorCS"),sQuery(id+"F0.wireOp",EDGE,"E22.106.MirrorCS"),sQuery(id+"F0.wireOp",EDGE,"E22.108.MirrorCS"),sQuery(id+"F0.wireOp",EDGE,"E22.109.MirrorCS"),sQuery(id+"F0.wireOp",EDGE,"E22.111.MirrorCS"),sQuery(id+"F0.wireOp",EDGE,"E22.112.MirrorCS"),sQuery(id+"F0.wireOp",EDGE,"E22.113.MirrorCS"),sQuery(id+"F0.wireOp",EDGE,"E22.114.MirrorCS"),sQuery(id+"F0.wireOp",EDGE,"E22.118.MirrorCS"),sQuery(id+"F0.wireOp",EDGE,"E22.120.MirrorCS"),sQuery(id+"F0.wireOp",EDGE,"E22.121.MirrorCS"),sQuery(id+"F0.wireOp",EDGE,"E22.122.MirrorCS"),sQuery(id+"F0.wireOp",EDGE,"E22.123.MirrorCS"),sQuery(id+"F0.wireOp",EDGE,"E22.127.MirrorCS"),sQuery(id+"F0.wireOp",EDGE,"E22.132.MirrorCS")])],"isStart":false});
            var sketch = newSketch(context, id + "F2", { "sketchPlane" : qUnion([Q0])});
            skLineSegment(sketch, "E23", {"start": v(-3, 9.5) * mm, "end": v(3, 9.5) * mm});
            skPoint(sketch, "E24", {"position": v(-9.56, 9.56) * mm});
            skLineSegment(sketch, "E25", {"start": v(0, 0) * mm, "end": v(-9.56, 9.56) * mm, "construction": true});
            skLineSegment(sketch, "E26", {"start": v(-9.56, 9.56) * mm, "end": v(-14.07, 14.07) * mm, "construction": true});
            skLineSegment(sketch, "E27", {"start": v(-9.56, 9.56) * mm, "end": v(-9.56, 11.06) * mm});
            skLineSegment(sketch, "E28", {"start": v(-9.56, 11.06) * mm, "end": v(-11.06, 11.06) * mm});
            skLineSegment(sketch, "E29", {"start": v(-11.06, 11.06) * mm, "end": v(-9.56, 9.56) * mm});
            skLineSegment(sketch, "E30.0.MirrorCS", {"start": v(11.06, 11.06) * mm, "end": v(9.56, 9.56) * mm});
            skLineSegment(sketch, "E31.0.MirrorCS", {"start": v(9.56, 11.06) * mm, "end": v(11.06, 11.06) * mm});
            skLineSegment(sketch, "E32.0.MirrorCS", {"start": v(9.56, 9.56) * mm, "end": v(9.56, 11.06) * mm});
            skLineSegment(sketch, "E33", {"start": v(-9.56, 11.06) * mm, "end": v(9.56, 11.06) * mm});
            skLineSegment(sketch, "E34", {"start": v(-9.56, 11.06) * mm, "end": v(-9.56, 12.06) * mm});
            skLineSegment(sketch, "E35", {"start": v(-9.56, 12.06) * mm, "end": v(-7.56, 12.06) * mm});
            skLineSegment(sketch, "E36", {"start": v(-7.56, 12.06) * mm, "end": v(-7.56, 11.06) * mm});
            skLineSegment(sketch, "E37.0.MirrorCS", {"start": v(7.56, 12.06) * mm, "end": v(7.56, 11.06) * mm});
            skLineSegment(sketch, "E38.0.MirrorCS", {"start": v(9.56, 12.06) * mm, "end": v(7.56, 12.06) * mm});
            skLineSegment(sketch, "E39.0.MirrorCS", {"start": v(9.56, 11.06) * mm, "end": v(9.56, 12.06) * mm});
            skLineSegment(sketch, "E40", {"start": v(-3, 8.5) * mm, "end": v(3, 8.5) * mm});
            skSolve(sketch);
        }
        {
            var Q0;
            Q0=makeQuery(id+"F2.imprint","IMPRINT",FACE,{"disambiguationData":[TD([[makeQuery(id+"F2.imprint","IMPRINT",EDGE,{"derivedFrom":sQuery(id+"F2.wireOp",EDGE,"E23")}),1.0]])]});
            var Q1;
            {var subQ1=sQuery(id+"F2.wireOp",EDGE,"E34");Q1=makeQuery(id+"F2.imprint","IMPRINT",FACE,{"disambiguationData":[TD([[makeQuery(id+"F2.imprint","IMPRINT",EDGE,{"derivedFrom":subQ1}),-1.0]])]});}
            var Q2;
            {var subQ1=sQuery(id+"F2.wireOp",EDGE,"E37.0.MirrorCS");Q2=makeQuery(id+"F2.imprint","IMPRINT",FACE,{"disambiguationData":[TD([[makeQuery(id+"F2.imprint","IMPRINT",EDGE,{"derivedFrom":subQ1}),1.0]])]});}
            extrude(context, id + "F3", {"entities" : qUnion([Q0, Q1, Q2]), "oppositeDirection" : true, "depth" : 20 * mm});
        }
        {
            var Q0;
            Q0=makeQuery(id+"F3.opExtrude","SWEPT_EDGE",EDGE,{"disambiguationData":[OSD([sQuery(id+"F0.wireOp",EDGE,"E21.22.MirrorCS"),sQuery(id+"F0.wireOp",EDGE,"E21.28.MirrorCS")])]});
            var Q1;
            Q1=makeQuery(id+"F3.opExtrude","SWEPT_EDGE",EDGE,{"disambiguationData":[OSD([sQuery(id+"F0.wireOp",EDGE,"E22.55.MirrorCS"),sQuery(id+"F0.wireOp",EDGE,"E22.58.MirrorCS")])]});
            var Q2;
            Q2=makeQuery(id+"F3.opExtrude","SWEPT_EDGE",EDGE,{"disambiguationData":[OSD([sQuery(id+"F2.wireOp",EDGE,"E35"),sQuery(id+"F2.wireOp",EDGE,"E36")])]});
            var Q3;
            Q3=makeQuery(id+"F3.opExtrude","SWEPT_EDGE",EDGE,{"disambiguationData":[OSD([sQuery(id+"F2.wireOp",EDGE,"E37.0.MirrorCS"),sQuery(id+"F2.wireOp",EDGE,"E38.0.MirrorCS")])]});
            fillet(context, id + "F4", {"entities" : qUnion([Q0, Q1, Q2, Q3]), "radius" : 0.2 * mm, "tangentPropagation" : true, "allowEdgeOverflow" : false});
        }
        {
            var Q0;
            Q0=makeQuery(id+"F2.imprint","IMPRINT",FACE,{"disambiguationData":[TD([[makeQuery(id+"F2.imprint","IMPRINT",EDGE,{"derivedFrom":sQuery(id+"F2.wireOp",EDGE,"E23")}),-1.0]])]});
            extrude(context, id + "F5", {"entities" : qUnion([Q0]), "oppositeDirection" : true, "depth" : 2.5 * mm});
        }
        {
            var Q0;
            Q0=makeQuery(id+"F5.opExtrude","CAP_EDGE",EDGE,{"disambiguationData":[OSD([sQuery(id+"F2.wireOp",EDGE,"E40")])],"isStart":false});
            chamfer(context, id + "F6", {"entities" : qUnion([Q0]), "chamferType" : ChamferType.TWO_OFFSETS, "width1" : 1.5 * mm, "oppositeDirection" : false, "width2" : 1 * mm, "tangentPropagation" : true});
        }
        {
            var Q0;
            Q0=makeQuery(id+"F3.opExtrude","SWEPT_FACE",FACE,{"disambiguationData":[OSD([sQuery(id+"F0.wireOp",EDGE,"E21.49.MirrorCS")])]});
            var sketch = newSketch(context, id + "F7", { "sketchPlane" : qUnion([Q0])});
            skLineSegment(sketch, "E41", {"start": v(-8.5, 15) * mm, "end": v(7.97, 15) * mm, "construction": true});
            skSolve(sketch);
        }
        {
            var Q0;
            Q0=sQuery(id+"F7.wireOp",EDGE,"E41");
            cPlane(context, id + "F8", {"entities" : qUnion([Q0]), "cplaneType" : CPlaneType.LINE_ANGLE, "offset" : 150 * mm, "angle" : 90 * degree, "width" : 150 * mm, "height" : 150 * mm});
        }
        {
            var Q0;
            Q0=makeQuery(id+"F5.opExtrude","SWEPT_BODY",BODY,{"disambiguationData":[OSD([sQuery(id+"F0.wireOp",EDGE,"E21.46.MirrorCS"),sQuery(id+"F0.wireOp",EDGE,"E22.59.MirrorCS"),sQuery(id+"F2.wireOp",EDGE,"E23"),sQuery(id+"F2.wireOp",EDGE,"E40")])]});
            var Q1;
            Q1=qCreatedBy(id+"F8.planeOp",FACE);
            mirror(context, id + "F9", {"entities" : qUnion([Q0]), "mirrorPlane" : qUnion([Q1])});
        }
        {
            var Q0;
            Q0=makeQuery(id+"F3.opExtrude","SWEPT_FACE",FACE,{"disambiguationData":[OSD([sQuery(id+"F2.wireOp",EDGE,"E33")])]});
            var sketch = newSketch(context, id + "F10", { "sketchPlane" : qUnion([Q0])});
            skLineSegment(sketch, "E42", {"start": v(0, 5) * mm, "end": v(0, 23.33) * mm, "construction": true});
            skCircle(sketch, "E43", {"center": v(0, 15.03) * mm, "radius": 2.15 * mm});
            skSolve(sketch);
        }
        {
            var Q0;
            Q0=makeQuery(id+"F10.imprint","IMPRINT",FACE,{"disambiguationData":[TD([[makeQuery(id+"F10.imprint","IMPRINT",EDGE,{"derivedFrom":sQuery(id+"F10.wireOp",EDGE,"E43")}),1.0]])]});
            extrude(context, id + "F11", {"entities" : qUnion([Q0]), "operationType" : NewBodyOperationType.REMOVE, "oppositeDirection" : true, "depth" : 25 * mm});
        }
        {
            var Q0;
            Q0=makeQuery(id+"F11.boolean.opBoolean","COPY",FACE,{"derivedFrom":makeQuery(id+"F11.opExtrude","SWEPT_FACE",FACE,{"disambiguationData":[OSD([sQuery(id+"F10.wireOp",EDGE,"E43")])]})});
            fillet(context, id + "F12", {"entities" : qUnion([Q0]), "radius" : 0.2 * mm, "tangentPropagation" : true, "allowEdgeOverflow" : false});
        }
        {
            var Q0;
            Q0=makeQuery(id+"F3.opExtrude","SWEPT_FACE",FACE,{"disambiguationData":[OSD([sQuery(id+"F2.wireOp",EDGE,"E33")])]});
            var sketch = newSketch(context, id + "F13", { "sketchPlane" : qUnion([Q0])});
            skLineSegment(sketch, "E44.rect.bottom", {"start": v(7.56, 7.53) * mm, "end": v(-7.56, 7.53) * mm});
            skLineSegment(sketch, "E44.rect.top", {"start": v(7.56, 22.53) * mm, "end": v(-7.56, 22.53) * mm});
            skLineSegment(sketch, "E44.rect.left", {"start": v(7.56, 7.53) * mm, "end": v(7.56, 22.53) * mm});
            skLineSegment(sketch, "E44.rect.right", {"start": v(-7.56, 7.53) * mm, "end": v(-7.56, 22.53) * mm});
            skPoint(sketch, "E44.rect.middle", {"position": v(0, 15.03) * mm});
            skCircle(sketch, "E45", {"center": v(0, 15.03) * mm, "radius": 3.65 * mm});
            skSolve(sketch);
        }
        {
            var Q0;
            Q0=makeQuery(id+"F13.imprint","IMPRINT",FACE,{"disambiguationData":[TD([[makeQuery(id+"F13.imprint","IMPRINT",EDGE,{"derivedFrom":sQuery(id+"F13.wireOp",EDGE,"E44.rect.bottom")}),-1.0]])]});
            extrude(context, id + "F14", {"entities" : qUnion([Q0]), "depth" : 6 * mm});
        }
        {
            var Q0;
            Q0=makeQuery(id+"F13.imprint","IMPRINT",FACE,{"disambiguationData":[TD([[makeQuery(id+"F13.imprint","IMPRINT",EDGE,{"derivedFrom":sQuery(id+"F13.wireOp",EDGE,"E45")}),1.0]])]});
            extrude(context, id + "F15", {"entities" : qUnion([Q0]), "operationType" : NewBodyOperationType.ADD, "depth" : 2 * mm});
        }
        {
            var Q0;
            Q0=makeQuery(id+"F14.opExtrude","SWEPT_FACE",FACE,{"disambiguationData":[OSD([sQuery(id+"F13.wireOp",EDGE,"E44.rect.left")])]});
            var sketch = newSketch(context, id + "F16", { "sketchPlane" : qUnion([Q0])});
            skLineSegment(sketch, "E46.bottom", {"start": v(-17.06, 7.53) * mm, "end": v(-32.06, 7.53) * mm});
            skLineSegment(sketch, "E46.top", {"start": v(-17.06, 22.53) * mm, "end": v(-32.06, 22.53) * mm});
            skLineSegment(sketch, "E46.left", {"start": v(-17.06, 7.53) * mm, "end": v(-17.06, 22.53) * mm});
            skLineSegment(sketch, "E46.right", {"start": v(-32.06, 7.53) * mm, "end": v(-32.06, 22.53) * mm});
            skLineSegment(sketch, "E47", {"start": v(-17.06, 15.03) * mm, "end": v(-32.06, 15.03) * mm, "construction": true});
            skCircle(sketch, "E48", {"center": v(-24.56, 15.03) * mm, "radius": 6.1 * mm});
            skSolve(sketch);
        }
        {
            var Q0;
            Q0=makeQuery(id+"F16.imprint","IMPRINT",FACE,{"disambiguationData":[TD([[makeQuery(id+"F16.imprint","IMPRINT",EDGE,{"derivedFrom":sQuery(id+"F16.wireOp",EDGE,"E46.bottom")}),-1.0]])]});
            var Q1;
            Q1=makeQuery(id+"F14.opExtrude","SWEPT_FACE",FACE,{"disambiguationData":[OSD([sQuery(id+"F13.wireOp",EDGE,"E44.rect.right")])]});
            extrude(context, id + "F17", {"entities" : qUnion([Q0]), "operationType" : NewBodyOperationType.ADD, "endBound" : BoundingType.UP_TO_SURFACE, "oppositeDirection" : true, "endBoundEntityFace" : qUnion([Q1]), "depth" : 25 * mm});
        }
        {
            var Q0;
            Q0=makeQuery(id+"F15.opExtrude","CAP_FACE",FACE,{"disambiguationData":[OSD([sQuery(id+"F2.wireOp",EDGE,"E33"),sQuery(id+"F10.wireOp",EDGE,"E43"),sQuery(id+"F13.wireOp",EDGE,"E45")])],"isStart":false});
            extrude(context, id + "F18", {"entities" : qUnion([Q0]), "operationType" : NewBodyOperationType.REMOVE, "depth" : 25 * mm});
        }
        {
            var Q0;
            Q0=makeQuery(id+"F15.opExtrude","CAP_FACE",FACE,{"disambiguationData":[OSD([sQuery(id+"F2.wireOp",EDGE,"E33"),sQuery(id+"F10.wireOp",EDGE,"E43"),sQuery(id+"F13.wireOp",EDGE,"E45")])],"isStart":false});
            var sketch = newSketch(context, id + "F19", { "sketchPlane" : qUnion([Q0])});
            skCircle(sketch, "E49", {"center": v(0, 15.03) * mm, "radius": 3.65 * mm});
            skSolve(sketch);
        }
        {
            var Q0;
            {var subQ0=makeQuery(id+"F19.imprint","IMPRINT",EDGE,{"derivedFrom":makeQuery(id+"F15.opExtrude","CAP_EDGE",EDGE,{"disambiguationData":[OSD([sQuery(id+"F2.wireOp",EDGE,"E33"),sQuery(id+"F10.wireOp",EDGE,"E43")])],"isStart":false})});Q0=qUnion([makeQuery(id+"F19.imprint","IMPRINT",FACE,{"disambiguationData":[TD([[makeQuery(id+"F19.imprint","IMPRINT",EDGE,{"derivedFrom":sQuery(id+"F19.wireOp",EDGE,"E49")}),1.0]])]}),makeQuery(id+"F19.imprint","IMPRINT",FACE,{"disambiguationData":[TD([[subQ0,-1.0]])]})]);}
            var Q1;
            Q1=makeQuery(id+"F17.opExtrude","SWEPT_FACE",FACE,{"disambiguationData":[OSD([sQuery(id+"F16.wireOp",EDGE,"E48")])]});
            extrude(context, id + "F20", {"entities" : qUnion([Q0]), "operationType" : NewBodyOperationType.REMOVE, "endBound" : BoundingType.UP_TO_SURFACE, "endBoundEntityFace" : qUnion([Q1]), "depth" : 25 * mm});
        }
        {
            var Q0;
            Q0=makeQuery(id+"F17.opExtrude","SWEPT_FACE",FACE,{"disambiguationData":[OSD([sQuery(id+"F16.wireOp",EDGE,"E46.right")])]});
            var sketch = newSketch(context, id + "F21", { "sketchPlane" : qUnion([Q0])});
            skLineSegment(sketch, "E50", {"start": v(0, 22.53) * mm, "end": v(0, 7.53) * mm, "construction": true});
            skLineSegment(sketch, "E51", {"start": v(7.56, 15.03) * mm, "end": v(-7.56, 15.03) * mm, "construction": true});
            skCircle(sketch, "E52", {"center": v(0, 15.03) * mm, "radius": 1.7 * mm});
            skSolve(sketch);
        }
        {
            var Q0;
            Q0=makeQuery(id+"F21.imprint","IMPRINT",FACE,{"disambiguationData":[TD([[makeQuery(id+"F21.imprint","IMPRINT",EDGE,{"derivedFrom":sQuery(id+"F21.wireOp",EDGE,"E52")}),1.0]])]});
            extrude(context, id + "F22", {"entities" : qUnion([Q0]), "operationType" : NewBodyOperationType.REMOVE, "oppositeDirection" : true, "depth" : 25 * mm});
        }
        {
            var Q0;
            Q0=makeQuery(id+"F17.opExtrude","SWEPT_EDGE",EDGE,{"disambiguationData":[OSD([sQuery(id+"F16.wireOp",EDGE,"E46.top"),sQuery(id+"F16.wireOp",EDGE,"E46.right")])]});
            var Q1;
            Q1=makeQuery(id+"F17.opExtrude","SWEPT_EDGE",EDGE,{"disambiguationData":[OSD([sQuery(id+"F16.wireOp",EDGE,"E46.bottom"),sQuery(id+"F16.wireOp",EDGE,"E46.right")])]});
            fillet(context, id + "F23", {"entities" : qUnion([Q0, Q1]), "radius" : 6 * mm, "tangentPropagation" : true, "allowEdgeOverflow" : false});
        }
    });
